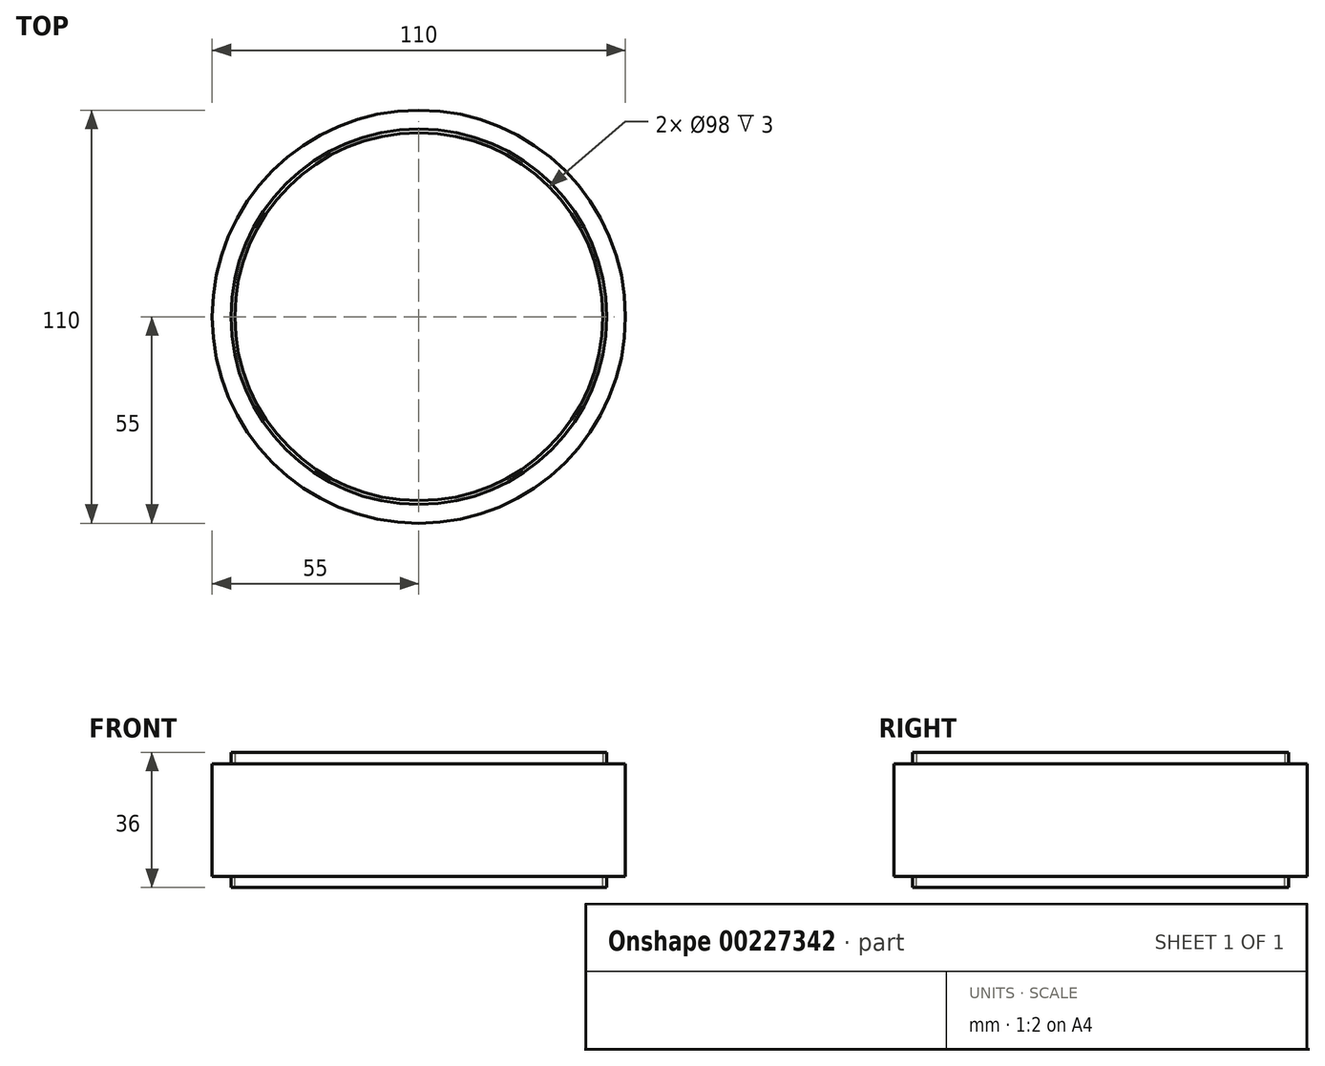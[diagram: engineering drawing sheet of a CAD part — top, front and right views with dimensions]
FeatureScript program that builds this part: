
annotation { "Feature Type Name" : "Feature", "Feature Type Description" : "" }
export const myFeature = defineFeature(function(context is Context, id is Id, definition is map)
    precondition{}
    {
        {
            var Q0;
            Q0=qCreatedBy(makeId("Top.planeOp"),FACE);
            var sketch = newSketch(context, id + "F0", { "sketchPlane" : qUnion([Q0])});
            skCircle(sketch, "E0", {"center": v(0, 0) * mm, "radius": 55 * mm});
            skSolve(sketch);
        }
        {
            var Q0;
            Q0 = qSketchRegion(id + "F0", true);
            extrude(context, id + "F1", {"entities" : qUnion([Q0]), "depth" : 30 * mm});
        }
        {
            var Q0;
            Q0=makeQuery(id+"F1.opExtrude","CAP_FACE",FACE,{"disambiguationData":[OSD([sQuery(id+"F0.wireOp",EDGE,"E0")])],"isStart":true});
            var sketch = newSketch(context, id + "F2", { "sketchPlane" : qUnion([Q0])});
            skCircle(sketch, "E1.0", {"center": v(0, 0) * mm, "radius": 50 * mm});
            skCircle(sketch, "E2.0", {"center": v(0, 0) * mm, "radius": 49 * mm});
            skSolve(sketch);
        }
        {
            var Q0;
            Q0=makeQuery(id+"F2.imprint","IMPRINT",FACE,{"disambiguationData":[TD([[makeQuery(id+"F2.imprint","IMPRINT",EDGE,{"derivedFrom":sQuery(id+"F2.wireOp",EDGE,"E1.0")}),1.0]])]});
            extrude(context, id + "F3", {"entities" : qUnion([Q0]), "operationType" : NewBodyOperationType.ADD, "depth" : 3 * mm});
        }
        {
            var Q0;
            Q0=makeQuery(id+"F1.opExtrude","CAP_FACE",FACE,{"disambiguationData":[OSD([sQuery(id+"F0.wireOp",EDGE,"E0")])],"isStart":false});
            var sketch = newSketch(context, id + "F4", { "sketchPlane" : qUnion([Q0])});
            skCircle(sketch, "E3.0", {"center": v(0, 0) * mm, "radius": 50 * mm});
            skCircle(sketch, "E4.0", {"center": v(0, 0) * mm, "radius": 49 * mm});
            skSolve(sketch);
        }
        {
            var Q0;
            Q0=makeQuery(id+"F4.imprint","IMPRINT",FACE,{"disambiguationData":[TD([[makeQuery(id+"F4.imprint","IMPRINT",EDGE,{"derivedFrom":sQuery(id+"F4.wireOp",EDGE,"E3.0")}),1.0]])]});
            extrude(context, id + "F5", {"entities" : qUnion([Q0]), "operationType" : NewBodyOperationType.ADD, "depth" : 3 * mm});
        }
    });
